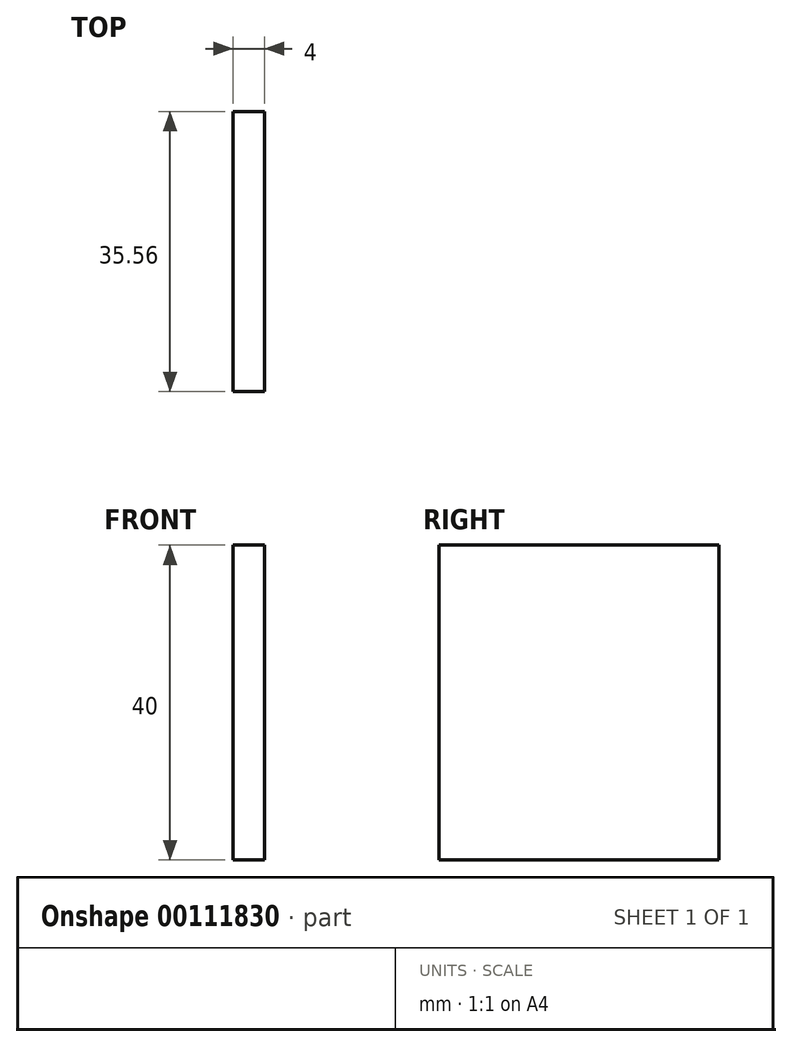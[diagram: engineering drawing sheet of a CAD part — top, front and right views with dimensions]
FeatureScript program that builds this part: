
annotation { "Feature Type Name" : "Feature", "Feature Type Description" : "" }
export const myFeature = defineFeature(function(context is Context, id is Id, definition is map)
    precondition{}
    {
        {
            var Q0;
            Q0=qCreatedBy(makeId("Front.planeOp"),FACE);
            var sketch = newSketch(context, id + "F0", { "sketchPlane" : qUnion([Q0])});
            skLineSegment(sketch, "E0", {"start": v(0, 0) * mm, "end": v(4, 0) * mm});
            skLineSegment(sketch, "E1", {"start": v(0, 0) * mm, "end": v(0, 40) * mm});
            skLineSegment(sketch, "E2", {"start": v(4, 0) * mm, "end": v(4, 40) * mm});
            skLineSegment(sketch, "E3", {"start": v(4, 40) * mm, "end": v(0, 40) * mm});
            skSolve(sketch);
        }
        {
            var Q0;
            Q0=makeQuery(id+"F0.imprint","IMPRINT",FACE,{"disambiguationData":[TD([[makeQuery(id+"F0.imprint","IMPRINT",EDGE,{"derivedFrom":sQuery(id+"F0.wireOp",EDGE,"E0")}),1.0]])]});
            extrude(context, id + "F1", {"entities" : qUnion([Q0]), "oppositeDirection" : true, "depth" : 35.56 * mm});
        }
    });
